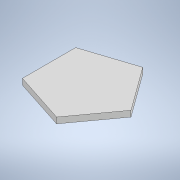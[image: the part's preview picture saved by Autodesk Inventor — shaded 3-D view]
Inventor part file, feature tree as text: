
AUTODESK INVENTOR PART (.ipt)
format: ipt  version: 2022.3 (Build 263350000, 350)  size: 92,672 bytes
history: native  units: in
note: dims shown in document units (in); Inventor stores cm internally (conversion verified against a paired STEP export)
features: extrude x1, sketch x1
ambient origin geometry x8: Origin, YZ Plane, XZ Plane, XY Plane, X Axis, Y Axis, Z Axis, Center Point
bodies: Solid1 (feature_tree)
feature tree (2):
  extrude  "Extrusion1"  Depth=0.1575in
  sketch  "Sketch1"  dims[d1=0.1575in d2=0.0in d3=0.0197in d4=0.0344in]
